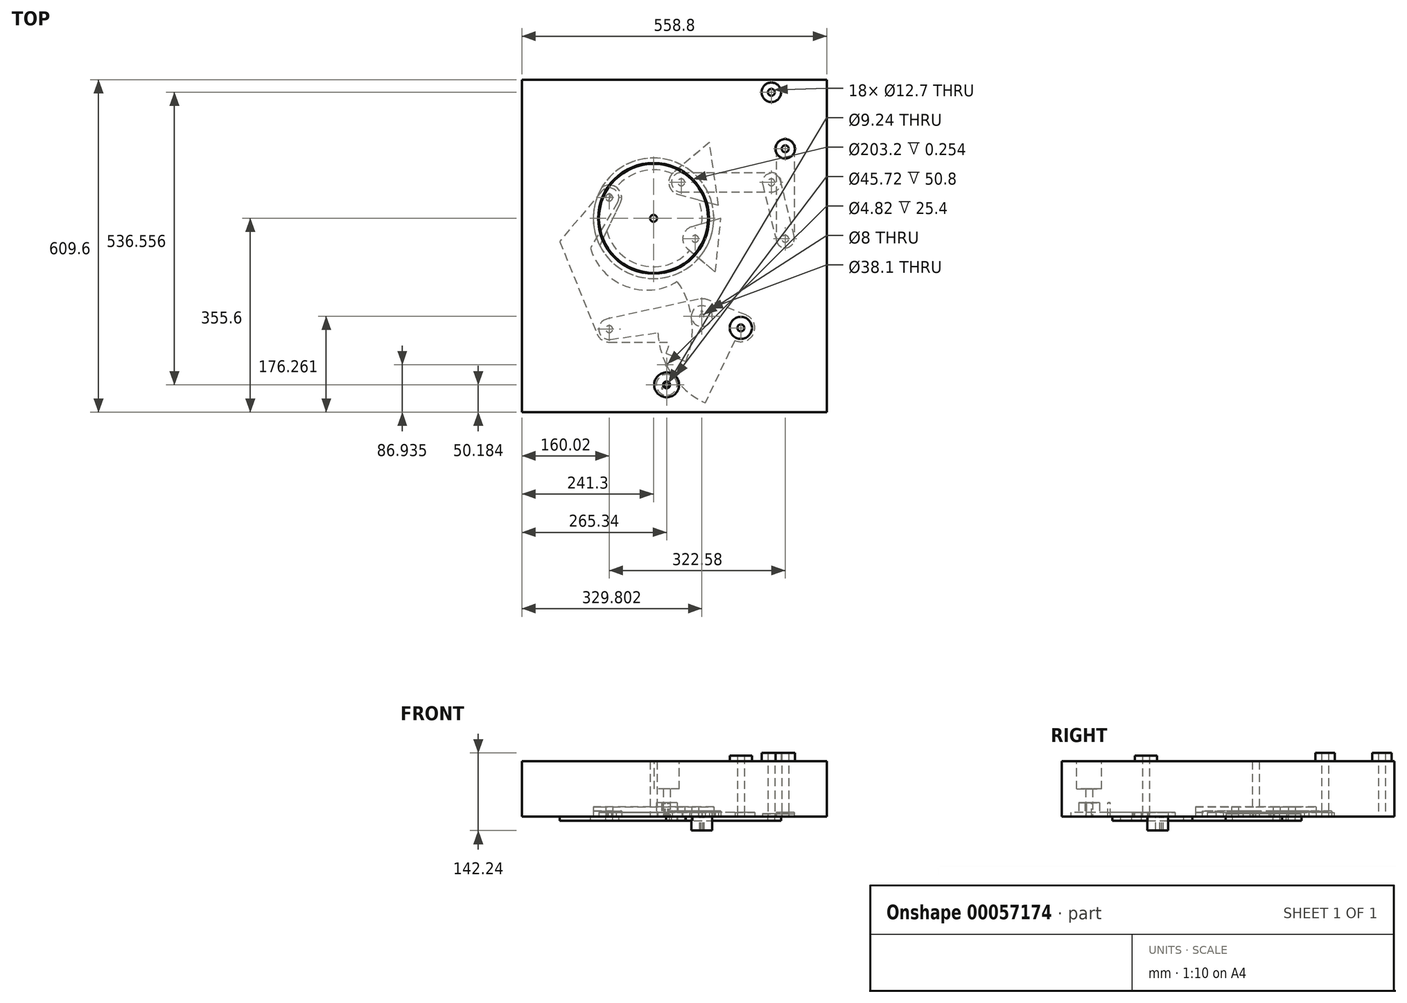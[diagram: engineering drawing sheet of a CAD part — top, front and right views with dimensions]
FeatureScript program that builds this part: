
annotation { "Feature Type Name" : "Feature", "Feature Type Description" : "" }
export const myFeature = defineFeature(function(context is Context, id is Id, definition is map)
    precondition{}
    {
        {
            var Q0;
            Q0=qCreatedBy(makeId("Top.planeOp"),FACE);
            var sketch = newSketch(context, id + "F0", { "sketchPlane" : qUnion([Q0])});
            skCircle(sketch, "E0", {"center": v(0, 0) * mm, "radius": 100 * mm});
            skCircle(sketch, "E1", {"center": v(-100, 0) * mm, "radius": 100 * mm, "construction": true});
            skCircle(sketch, "E2", {"center": v(0, 100) * mm, "radius": 100 * mm, "construction": true});
            skCircle(sketch, "E3", {"center": v(100, 0) * mm, "radius": 100 * mm, "construction": true});
            skCircle(sketch, "E4", {"center": v(0, -100) * mm, "radius": 100 * mm, "construction": true});
            skLineSegment(sketch, "E5", {"start": v(0, 0) * mm, "end": v(0, 167.8) * mm, "construction": true});
            skLineSegment(sketch, "E6", {"start": v(-81.28, 38.1) * mm, "end": v(-81.28, -203.2) * mm, "construction": true});
            skLineSegment(sketch, "E7", {"start": v(-81.28, -203.2) * mm, "end": v(160, -200.98) * mm, "construction": true});
            skLineSegment(sketch, "E8", {"start": v(-81.28, 38.1) * mm, "end": v(160, -200.98) * mm, "construction": true});
            skArc(sketch, "E9", {"start": v(24.5, 13.68) * mm, "mid": v(-74.9, 38.02) * mm, "end": v(-175.43, 18.97) * mm, "construction": true});
            skArc(sketch, "E10", {"start": v(-57.83, -97.2) * mm, "mid": v(-81.25, -196.81) * mm, "end": v(-61.29, -297.17) * mm, "construction": true});
            skLineSegment(sketch, "E11", {"start": v(-175.43, 18.97) * mm, "end": v(-81.28, -203.2) * mm, "construction": true});
            skLineSegment(sketch, "E12", {"start": v(24.5, 13.68) * mm, "end": v(-81.28, -203.2) * mm, "construction": true});
            skLineSegment(sketch, "E13", {"start": v(-61.29, -297.17) * mm, "end": v(160, -200.98) * mm, "construction": true});
            skLineSegment(sketch, "E14", {"start": v(-57.83, -97.2) * mm, "end": v(160, -200.98) * mm, "construction": true});
            skLineSegment(sketch, "E15", {"start": v(-175.43, 18.97) * mm, "end": v(24.5, 13.68) * mm, "construction": true});
            skLineSegment(sketch, "E16", {"start": v(-57.83, -97.2) * mm, "end": v(-61.29, -297.17) * mm, "construction": true});
            skCircle(sketch, "E17", {"center": v(0, 0) * mm, "radius": 200 * mm, "construction": true});
            skLineSegment(sketch, "E18", {"start": v(50.8, 66.04) * mm, "end": v(215.9, 66.04) * mm, "construction": true});
            skLineSegment(sketch, "E19", {"start": v(215.9, 66.04) * mm, "end": v(215.9, 231.14) * mm, "construction": true});
            skLineSegment(sketch, "E20", {"start": v(76.2, -37.57) * mm, "end": v(241.3, -37.57) * mm, "construction": true});
            skLineSegment(sketch, "E21", {"start": v(241.3, -37.57) * mm, "end": v(241.3, 127.53) * mm, "construction": true});
            skLineSegment(sketch, "E22", {"start": v(50.8, 66.04) * mm, "end": v(76.2, -37.57) * mm, "construction": true});
            skLineSegment(sketch, "E23", {"start": v(215.9, 231.14) * mm, "end": v(241.3, 127.53) * mm, "construction": true});
            skLineSegment(sketch, "E24", {"start": v(215.9, 66.04) * mm, "end": v(241.3, -37.57) * mm, "construction": true});
            skSolve(sketch);
        }
        {
            var Q0;
            Q0=qCreatedBy(makeId("Top.planeOp"),FACE);
            var sketch = newSketch(context, id + "F1", { "sketchPlane" : qUnion([Q0])});
            skCircle(sketch, "E25", {"center": v(-81.28, 38.1) * mm, "radius": 17.78 * mm});
            skCircle(sketch, "E26", {"center": v(-81.28, -203.2) * mm, "radius": 23.86 * mm});
            skArc(sketch, "E27", {"start": v(59, -262.75) * mm, "mid": v(70.29, -187.27) * mm, "end": v(43.56, -115.79) * mm});
            skLineSegment(sketch, "E28", {"start": v(-81.28, -203.2) * mm, "end": v(43.56, -115.79) * mm, "construction": true});
            skLineSegment(sketch, "E29", {"start": v(-81.28, -203.2) * mm, "end": v(62.82, -252.82) * mm, "construction": true});
            skLineSegment(sketch, "E30", {"start": v(-66, 29.02) * mm, "end": v(-115.73, -54.74) * mm});
            skCircle(sketch, "E31", {"center": v(88.5, -179.34) * mm, "radius": 19.05 * mm});
            skLineSegment(sketch, "E32", {"start": v(88.5, -179.34) * mm, "end": v(-81.28, -203.2) * mm});
            skLineSegment(sketch, "E33", {"start": v(-94.9, 49.53) * mm, "end": v(-172, -42.36) * mm});
            skLineSegment(sketch, "E34", {"start": v(-172, -42.36) * mm, "end": v(-103.4, -212.14) * mm});
            skArc(sketch, "E35", {"start": v(-115.73, -54.74) * mm, "mid": v(-51.14, -124.55) * mm, "end": v(43.56, -115.79) * mm});
            skLineSegment(sketch, "E36", {"start": v(-81.28, -227.06) * mm, "end": v(29.52, -227.06) * mm});
            skArc(sketch, "E37", {"start": v(23.05, -247.49) * mm, "mid": v(26.77, -237.43) * mm, "end": v(29.52, -227.06) * mm});
            skLineSegment(sketch, "E38.trimOffspring", {"start": v(23.05, -247.49) * mm, "end": v(59, -262.75) * mm});
            skCircle(sketch, "E39", {"center": v(-81.28, -203.2) * mm, "radius": 6.35 * mm});
            skCircle(sketch, "E40", {"center": v(-81.28, 38.1) * mm, "radius": 6.35 * mm});
            skSolve(sketch);
        }
        {
            var Q0;
            Q0=qCreatedBy(makeId("Top.planeOp"),FACE);
            var sketch = newSketch(context, id + "F2", { "sketchPlane" : qUnion([Q0])});
            skCircle(sketch, "E41", {"center": v(160, -200.98) * mm, "radius": 25.4 * mm});
            skCircle(sketch, "E42", {"center": v(-81.28, -203.2) * mm, "radius": 19.05 * mm});
            skArc(sketch, "E43", {"start": v(7.87, -209.9) * mm, "mid": v(33.58, -286.07) * mm, "end": v(94.47, -338.56) * mm});
            skCircle(sketch, "E44", {"center": v(24.04, -305.42) * mm, "radius": 19.05 * mm});
            skLineSegment(sketch, "E45", {"start": v(160, -200.98) * mm, "end": v(24.04, -305.42) * mm, "construction": true});
            skLineSegment(sketch, "E46", {"start": v(10.18, -228.82) * mm, "end": v(160, -200.98) * mm, "construction": true});
            skCircle(sketch, "E47", {"center": v(88.5, -179.34) * mm, "radius": 31.75 * mm});
            skLineSegment(sketch, "E48", {"start": v(169.4, -177.38) * mm, "end": v(100.25, -149.84) * mm});
            skLineSegment(sketch, "E49", {"start": v(81.77, -148.31) * mm, "end": v(-85.32, -184.58) * mm});
            skLineSegment(sketch, "E50", {"start": v(-78.63, -222.06) * mm, "end": v(7.87, -209.9) * mm});
            skCircle(sketch, "E51", {"center": v(160, -200.98) * mm, "radius": 6.35 * mm});
            skCircle(sketch, "E52", {"center": v(88.5, -179.34) * mm, "radius": 19.05 * mm});
            skCircle(sketch, "E53", {"center": v(-81.28, -203.2) * mm, "radius": 6.35 * mm});
            skLineSegment(sketch, "E54", {"start": v(-81.28, -203.2) * mm, "end": v(88.5, -179.34) * mm, "construction": true});
            skLineSegment(sketch, "E55.trimOffspring", {"start": v(149.09, -223.9) * mm, "end": v(94.47, -338.56) * mm});
            skCircle(sketch, "E56", {"center": v(15.96, -311.62) * mm, "radius": 1.52 * mm});
            skCircle(sketch, "E57", {"center": v(24.04, -305.42) * mm, "radius": 4 * mm});
            skSolve(sketch);
        }
        {
            var Q0;
            Q0=qCreatedBy(makeId("Top.planeOp"),FACE);
            var sketch = newSketch(context, id + "F3", { "sketchPlane" : qUnion([Q0])});
            skLineSegment(sketch, "E58.bottom", {"start": v(-241.3, 254) * mm, "end": v(317.5, 254) * mm});
            skLineSegment(sketch, "E58.top", {"start": v(-241.3, -355.6) * mm, "end": v(317.5, -355.6) * mm});
            skLineSegment(sketch, "E58.left", {"start": v(-241.3, 254) * mm, "end": v(-241.3, -355.6) * mm});
            skLineSegment(sketch, "E58.right", {"start": v(317.5, 254) * mm, "end": v(317.5, -355.6) * mm});
            skCircle(sketch, "E59", {"center": v(24.04, -305.42) * mm, "radius": 6.35 * mm});
            skCircle(sketch, "E60", {"center": v(160, -200.98) * mm, "radius": 6.35 * mm});
            skCircle(sketch, "E61", {"center": v(0, 0) * mm, "radius": 6.35 * mm});
            skCircle(sketch, "E62", {"center": v(215.9, 231.14) * mm, "radius": 6.35 * mm});
            skCircle(sketch, "E63", {"center": v(241.3, 127.53) * mm, "radius": 6.35 * mm});
            skSolve(sketch);
        }
        {
            var Q0;
            {var subQ8=sQuery(id+"F1.wireOp",EDGE,"E30");Q0=makeQuery(id+"F1.imprint","IMPRINT",FACE,{"disambiguationData":[TD([[makeQuery(id+"F1.imprint","IMPRINT",EDGE,{"derivedFrom":subQ8}),-1.0]])]});}
            var Q1;
            {var subQ1=sQuery(id+"F1.wireOp",EDGE,"E36");Q1=makeQuery(id+"F1.imprint","IMPRINT",FACE,{"disambiguationData":[TD([[makeQuery(id+"F1.imprint","IMPRINT",EDGE,{"derivedFrom":subQ1}),1.0]])]});}
            var Q2;
            Q2=makeQuery(id+"F1.imprint","IMPRINT",FACE,{"disambiguationData":[TD([[makeQuery(id+"F1.imprint","IMPRINT",EDGE,{"derivedFrom":sQuery(id+"F1.wireOp",EDGE,"E39")}),-1.0]])]});
            var Q3;
            Q3=makeQuery(id+"F1.imprint","IMPRINT",FACE,{"disambiguationData":[TD([[makeQuery(id+"F1.imprint","IMPRINT",EDGE,{"derivedFrom":sQuery(id+"F1.wireOp",EDGE,"E40")}),-1.0]])]});
            extrude(context, id + "F4", {"entities" : qUnion([Q0, Q1, Q2, Q3]), "oppositeDirection" : true, "depth" : 7.62 * mm});
        }
        {
            var Q0;
            Q0=makeQuery(id+"F1.imprint","IMPRINT",FACE,{"disambiguationData":[TD([[makeQuery(id+"F1.imprint","IMPRINT",EDGE,{"derivedFrom":sQuery(id+"F1.wireOp",EDGE,"E31")}),1.0]])]});
            extrude(context, id + "F5", {"entities" : qUnion([Q0]), "oppositeDirection" : true, "depth" : 25.4 * mm});
        }
        {
            var Q0;
            {var subQ3=sQuery(id+"F2.wireOp",EDGE,"E48");Q0=makeQuery(id+"F2.imprint","IMPRINT",FACE,{"disambiguationData":[TD([[makeQuery(id+"F2.imprint","IMPRINT",EDGE,{"derivedFrom":subQ3}),1.0]])]});}
            var Q1;
            Q1=makeQuery(id+"F2.imprint","IMPRINT",FACE,{"disambiguationData":[TD([[makeQuery(id+"F2.imprint","IMPRINT",EDGE,{"derivedFrom":sQuery(id+"F2.wireOp",EDGE,"E53")}),-1.0]])]});
            var Q2;
            Q2=makeQuery(id+"F2.imprint","IMPRINT",FACE,{"disambiguationData":[TD([[makeQuery(id+"F2.imprint","IMPRINT",EDGE,{"derivedFrom":sQuery(id+"F2.wireOp",EDGE,"E52")}),-1.0]])]});
            var Q3;
            Q3=makeQuery(id+"F2.imprint","IMPRINT",FACE,{"disambiguationData":[TD([[makeQuery(id+"F2.imprint","IMPRINT",EDGE,{"derivedFrom":sQuery(id+"F2.wireOp",EDGE,"E51")}),-1.0]])]});
            extrude(context, id + "F6", {"entities" : qUnion([Q0, Q1, Q2, Q3]), "depth" : 7.62 * mm});
        }
        {
            var Q0;
            Q0=makeQuery(id+"F2.imprint","IMPRINT",FACE,{"disambiguationData":[TD([[makeQuery(id+"F2.imprint","IMPRINT",EDGE,{"derivedFrom":sQuery(id+"F2.wireOp",EDGE,"E44")}),1.0]])]});
            extrude(context, id + "F7", {"entities" : qUnion([Q0]), "depth" : 25.4 * mm});
        }
        {
            var Q0;
            Q0=makeQuery(id+"F3.imprint","IMPRINT",FACE,{"disambiguationData":[TD([[makeQuery(id+"F3.imprint","IMPRINT",EDGE,{"derivedFrom":sQuery(id+"F3.wireOp",EDGE,"E58.bottom")}),-1.0]])]});
            extrude(context, id + "F8", {"entities" : qUnion([Q0]), "depth" : 101.6 * mm});
        }
        {
            var Q0;
            Q0=makeQuery(id+"F8.opExtrude","CAP_FACE",FACE,{"disambiguationData":[OSD([sQuery(id+"F3.wireOp",EDGE,"E58.bottom"),sQuery(id+"F3.wireOp",EDGE,"E58.top"),sQuery(id+"F3.wireOp",EDGE,"E58.left"),sQuery(id+"F3.wireOp",EDGE,"E58.right"),sQuery(id+"F3.wireOp",EDGE,"E59"),sQuery(id+"F3.wireOp",EDGE,"E60"),sQuery(id+"F3.wireOp",EDGE,"E61")])],"isStart":false});
            var sketch = newSketch(context, id + "F9", { "sketchPlane" : qUnion([Q0])});
            skCircle(sketch, "E64", {"center": v(0, 0) * mm, "radius": 101.6 * mm});
            skCircle(sketch, "E65", {"center": v(0, 0) * mm, "radius": 100 * mm});
            skSolve(sketch);
        }
        {
            var Q0;
            Q0=qSketchRegion(id+"F9",true);
            extrude(context, id + "F10", {"entities" : qUnion([Q0]), "operationType" : NewBodyOperationType.REMOVE, "oppositeDirection" : true, "depth" : 0.25 * mm});
        }
        {
            var Q0;
            {var subQ0=sQuery(id+"F3.wireOp",EDGE,"E58.bottom");var subQ1=sQuery(id+"F3.wireOp",EDGE,"E58.top");var subQ2=sQuery(id+"F3.wireOp",EDGE,"E58.left");var subQ3=sQuery(id+"F3.wireOp",EDGE,"E58.right");var subQ4=sQuery(id+"F3.wireOp",EDGE,"E59");var subQ5=sQuery(id+"F3.wireOp",EDGE,"E60");Q0=makeQuery(id+"F10.boolean.opBoolean","SPLIT",FACE,{"disambiguationData":[TD([makeQuery(id+"F8.opExtrude","SWEPT_FACE",FACE,{"disambiguationData":[OSD([subQ0])]})])],"derivedFrom":makeQuery(id+"F8.opExtrude","CAP_FACE",FACE,{"disambiguationData":[OSD([subQ0,subQ1,subQ2,subQ3,subQ4,subQ5,sQuery(id+"F3.wireOp",EDGE,"E61")])],"isStart":false})});}
            var sketch = newSketch(context, id + "F11", { "sketchPlane" : qUnion([Q0])});
            skCircle(sketch, "E66", {"center": v(160, -200.98) * mm, "radius": 20.32 * mm});
            skCircle(sketch, "E67", {"center": v(160, -200.98) * mm, "radius": 6.35 * mm});
            skSolve(sketch);
        }
        {
            var Q0;
            Q0=qSketchRegion(id+"F11",true);
            extrude(context, id + "F12", {"entities" : qUnion([Q0]), "operationType" : NewBodyOperationType.ADD, "depth" : 10.16 * mm});
        }
        {
            var Q0;
            {var subQ0=sQuery(id+"F3.wireOp",EDGE,"E58.bottom");var subQ1=sQuery(id+"F3.wireOp",EDGE,"E58.top");var subQ2=sQuery(id+"F3.wireOp",EDGE,"E58.left");var subQ3=sQuery(id+"F3.wireOp",EDGE,"E58.right");var subQ4=sQuery(id+"F3.wireOp",EDGE,"E59");var subQ5=sQuery(id+"F3.wireOp",EDGE,"E60");Q0=makeQuery(id+"F10.boolean.opBoolean","SPLIT",FACE,{"disambiguationData":[TD([makeQuery(id+"F8.opExtrude","SWEPT_FACE",FACE,{"disambiguationData":[OSD([subQ0])]})])],"derivedFrom":makeQuery(id+"F8.opExtrude","CAP_FACE",FACE,{"disambiguationData":[OSD([subQ0,subQ1,subQ2,subQ3,subQ4,subQ5,sQuery(id+"F3.wireOp",EDGE,"E61")])],"isStart":false})});}
            var sketch = newSketch(context, id + "F13", { "sketchPlane" : qUnion([Q0])});
            skCircle(sketch, "E68", {"center": v(24.04, -305.42) * mm, "radius": 22.86 * mm});
            skSolve(sketch);
        }
        {
            var Q0;
            Q0=qSketchRegion(id+"F13",true);
            extrude(context, id + "F14", {"entities" : qUnion([Q0]), "operationType" : NewBodyOperationType.REMOVE, "oppositeDirection" : true, "depth" : 50.8 * mm});
        }
        {
            var Q0;
            Q0=makeQuery(id+"F7.opExtrude","CAP_FACE",FACE,{"disambiguationData":[OSD([sQuery(id+"F2.wireOp",EDGE,"E44")])],"isStart":false});
            var sketch = newSketch(context, id + "F15", { "sketchPlane" : qUnion([Q0])});
            skCircle(sketch, "E69", {"center": v(24.04, -305.42) * mm, "radius": 4.62 * mm});
            skCircle(sketch, "E70", {"center": v(24.04, -268.67) * mm, "radius": 2.41 * mm});
            skSolve(sketch);
        }
        {
            var Q0;
            Q0=qSketchRegion(id+"F15",true);
            extrude(context, id + "F16", {"entities" : qUnion([Q0]), "operationType" : NewBodyOperationType.REMOVE, "endBound" : BoundingType.THROUGH_ALL, "oppositeDirection" : true, "depth" : 25.4 * mm});
        }
        {
            var Q0;
            Q0=makeQuery(id+"F5.opExtrude","CAP_FACE",FACE,{"disambiguationData":[OSD([sQuery(id+"F1.wireOp",EDGE,"E31")])],"isStart":true});
            var sketch = newSketch(context, id + "F17", { "sketchPlane" : qUnion([Q0])});
            skCircle(sketch, "E71", {"center": v(88.5, -179.34) * mm, "radius": 4 * mm});
            skCircle(sketch, "E72", {"center": v(88.5, -170.8) * mm, "radius": 1.52 * mm});
            skLineSegment(sketch, "E73", {"start": v(88.5, -179.34) * mm, "end": v(88.5, -211.92) * mm, "construction": true});
            skSolve(sketch);
        }
        {
            var Q0;
            Q0=qSketchRegion(id+"F17",true);
            extrude(context, id + "F18", {"entities" : qUnion([Q0]), "operationType" : NewBodyOperationType.REMOVE, "endBound" : BoundingType.THROUGH_ALL, "oppositeDirection" : true, "depth" : 25.4 * mm});
        }
        {
            var Q0;
            Q0=qCreatedBy(makeId("Top.planeOp"),FACE);
            var sketch = newSketch(context, id + "F19", { "sketchPlane" : qUnion([Q0])});
            skCircle(sketch, "E74", {"center": v(0, 0) * mm, "radius": 110.5 * mm});
            skCircle(sketch, "E75", {"center": v(-81.28, 38.1) * mm, "radius": 6.35 * mm});
            skCircle(sketch, "E76", {"center": v(50.8, 66.04) * mm, "radius": 6.35 * mm});
            skCircle(sketch, "E77", {"center": v(76.2, -37.57) * mm, "radius": 6.35 * mm});
            skSolve(sketch);
        }
        {
            var Q0;
            Q0=qSketchRegion(id+"F19",true);
            extrude(context, id + "F20", {"entities" : qUnion([Q0]), "depth" : 17.78 * mm});
        }
        {
            var Q0;
            Q0=makeQuery(id+"F20.opExtrude","CAP_FACE",FACE,{"disambiguationData":[OSD([sQuery(id+"F19.wireOp",EDGE,"E74"),sQuery(id+"F19.wireOp",EDGE,"E75")])],"isStart":true});
            var sketch = newSketch(context, id + "F21", { "sketchPlane" : qUnion([Q0])});
            skCircle(sketch, "E78", {"center": v(-81.28, -38.1) * mm, "radius": 22.86 * mm});
            skLineSegment(sketch, "E79", {"start": v(-98.6, 49.85) * mm, "end": v(-60.72, -28.1) * mm});
            skArc(sketch, "E80", {"start": v(-98.6, 49.85) * mm, "mid": v(-110.43, -3.71) * mm, "end": v(-95.04, -56.36) * mm});
            skLineSegment(sketch, "E81", {"start": v(0, 0) * mm, "end": v(-64.6, 0) * mm});
            skSolve(sketch);
        }
        {
            var Q0;
            Q0=makeQuery(id+"F21.imprint","IMPRINT",FACE,{"disambiguationData":[TD([[makeQuery(id+"F21.imprint","IMPRINT",EDGE,{"derivedFrom":makeQuery(id+"F20.opExtrude","CAP_EDGE",EDGE,{"disambiguationData":[OSD([sQuery(id+"F19.wireOp",EDGE,"E75")])],"isStart":true})}),1.0]])]});
            var Q1;
            {var subQ3=sQuery(id+"F21.wireOp",EDGE,"E79");Q1=makeQuery(id+"F21.imprint","IMPRINT",FACE,{"disambiguationData":[TD([[makeQuery(id+"F21.imprint","IMPRINT",EDGE,{"derivedFrom":subQ3}),-1.0]])]});}
            extrude(context, id + "F22", {"entities" : qUnion([Q0, Q1]), "operationType" : NewBodyOperationType.REMOVE, "oppositeDirection" : true, "depth" : 10.16 * mm});
        }
        {
            var Q0;
            Q0=makeQuery(id+"F20.opExtrude","CAP_FACE",FACE,{"disambiguationData":[OSD([sQuery(id+"F19.wireOp",EDGE,"E74"),sQuery(id+"F19.wireOp",EDGE,"E75")])],"isStart":true});
            var sketch = newSketch(context, id + "F23", { "sketchPlane" : qUnion([Q0])});
            skCircle(sketch, "E82", {"center": v(0, 0) * mm, "radius": 88.9 * mm});
            skCircle(sketch, "E83", {"center": v(0, 0) * mm, "radius": 110.5 * mm});
            skSolve(sketch);
        }
        {
            var Q0;
            Q0=qSketchRegion(id+"F23",true);
            extrude(context, id + "F24", {"entities" : qUnion([Q0]), "operationType" : NewBodyOperationType.REMOVE, "oppositeDirection" : true, "depth" : 7.62 * mm});
        }
        {
            var Q0;
            Q0=qCreatedBy(makeId("Top.planeOp"),FACE);
            var sketch = newSketch(context, id + "F25", { "sketchPlane" : qUnion([Q0])});
            skCircle(sketch, "E84", {"center": v(50.8, 66.04) * mm, "radius": 17.78 * mm});
            skCircle(sketch, "E85", {"center": v(215.9, 66.04) * mm, "radius": 17.78 * mm});
            skLineSegment(sketch, "E86", {"start": v(50.8, 83.82) * mm, "end": v(215.9, 83.82) * mm});
            skLineSegment(sketch, "E87", {"start": v(50.8, 48.26) * mm, "end": v(215.9, 48.26) * mm});
            skCircle(sketch, "E88", {"center": v(50.8, 66.04) * mm, "radius": 6.35 * mm});
            skCircle(sketch, "E89", {"center": v(215.9, 66.04) * mm, "radius": 6.35 * mm});
            skSolve(sketch);
        }
        {
            var Q0;
            Q0=qCreatedBy(makeId("Top.planeOp"),FACE);
            var sketch = newSketch(context, id + "F26", { "sketchPlane" : qUnion([Q0])});
            skCircle(sketch, "E90", {"center": v(241.3, -37.57) * mm, "radius": 16.5 * mm});
            skCircle(sketch, "E91", {"center": v(241.3, 127.53) * mm, "radius": 16.51 * mm});
            skLineSegment(sketch, "E92", {"start": v(257.81, 127.53) * mm, "end": v(257.8, -37.57) * mm});
            skLineSegment(sketch, "E93", {"start": v(224.8, 127.53) * mm, "end": v(224.8, -37.57) * mm});
            skCircle(sketch, "E94", {"center": v(241.3, 127.53) * mm, "radius": 6.35 * mm});
            skCircle(sketch, "E95", {"center": v(241.3, -37.57) * mm, "radius": 6.35 * mm});
            skSolve(sketch);
        }
        {
            var Q0;
            Q0=qCreatedBy(makeId("Top.planeOp"),FACE);
            var sketch = newSketch(context, id + "F27", { "sketchPlane" : qUnion([Q0])});
            skCircle(sketch, "E96", {"center": v(215.9, 66.04) * mm, "radius": 16.51 * mm});
            skCircle(sketch, "E97", {"center": v(241.3, -37.57) * mm, "radius": 16.51 * mm});
            skLineSegment(sketch, "E98", {"start": v(231.94, 69.97) * mm, "end": v(257.34, -33.64) * mm});
            skLineSegment(sketch, "E99", {"start": v(199.86, 62.1) * mm, "end": v(225.26, -41.5) * mm});
            skCircle(sketch, "E100", {"center": v(215.9, 66.04) * mm, "radius": 6.35 * mm});
            skCircle(sketch, "E101", {"center": v(241.3, -37.57) * mm, "radius": 6.35 * mm});
            skSolve(sketch);
        }
        {
            var Q0;
            Q0=makeQuery(id+"F25.imprint","IMPRINT",FACE,{"disambiguationData":[TD([[makeQuery(id+"F25.imprint","IMPRINT",EDGE,{"derivedFrom":sQuery(id+"F25.wireOp",EDGE,"E89")}),-1.0]])]});
            var Q1;
            {var subQ1=sQuery(id+"F25.wireOp",EDGE,"E86");Q1=makeQuery(id+"F25.imprint","IMPRINT",FACE,{"disambiguationData":[TD([[makeQuery(id+"F25.imprint","IMPRINT",EDGE,{"derivedFrom":subQ1}),-1.0]])]});}
            var Q2;
            Q2=makeQuery(id+"F25.imprint","IMPRINT",FACE,{"disambiguationData":[TD([[makeQuery(id+"F25.imprint","IMPRINT",EDGE,{"derivedFrom":sQuery(id+"F25.wireOp",EDGE,"E88")}),-1.0]])]});
            extrude(context, id + "F28", {"entities" : qUnion([Q0, Q1, Q2]), "oppositeDirection" : true, "depth" : 7.62 * mm});
        }
        {
            var Q0;
            Q0=makeQuery(id+"F26.imprint","IMPRINT",FACE,{"disambiguationData":[TD([[makeQuery(id+"F26.imprint","IMPRINT",EDGE,{"derivedFrom":sQuery(id+"F26.wireOp",EDGE,"E94")}),-1.0]])]});
            var Q1;
            {var subQ1=sQuery(id+"F26.wireOp",EDGE,"E92");Q1=makeQuery(id+"F26.imprint","IMPRINT",FACE,{"disambiguationData":[TD([[makeQuery(id+"F26.imprint","IMPRINT",EDGE,{"derivedFrom":subQ1}),-1.0]])]});}
            var Q2;
            Q2=makeQuery(id+"F26.imprint","IMPRINT",FACE,{"disambiguationData":[TD([[makeQuery(id+"F26.imprint","IMPRINT",EDGE,{"derivedFrom":sQuery(id+"F26.wireOp",EDGE,"E95")}),-1.0]])]});
            extrude(context, id + "F29", {"entities" : qUnion([Q0, Q1, Q2]), "depth" : 7.62 * mm});
        }
        {
            var Q0;
            Q0=makeQuery(id+"F27.imprint","IMPRINT",FACE,{"disambiguationData":[TD([[makeQuery(id+"F27.imprint","IMPRINT",EDGE,{"derivedFrom":sQuery(id+"F27.wireOp",EDGE,"E100")}),-1.0]])]});
            var Q1;
            {var subQ0=sQuery(id+"F27.wireOp",EDGE,"E98");Q1=makeQuery(id+"F27.imprint","IMPRINT",FACE,{"disambiguationData":[TD([[makeQuery(id+"F27.imprint","IMPRINT",EDGE,{"derivedFrom":subQ0}),-1.0]])]});}
            var Q2;
            Q2=makeQuery(id+"F27.imprint","IMPRINT",FACE,{"disambiguationData":[TD([[makeQuery(id+"F27.imprint","IMPRINT",EDGE,{"derivedFrom":sQuery(id+"F27.wireOp",EDGE,"E101")}),-1.0]])]});
            extrude(context, id + "F30", {"entities" : qUnion([Q0, Q1, Q2]), "depth" : 5.08 * mm});
        }
        {
            var Q0;
            {var subQ0=sQuery(id+"F3.wireOp",EDGE,"E58.bottom");var subQ1=sQuery(id+"F3.wireOp",EDGE,"E58.top");var subQ2=sQuery(id+"F3.wireOp",EDGE,"E58.left");var subQ3=sQuery(id+"F3.wireOp",EDGE,"E58.right");var subQ4=sQuery(id+"F3.wireOp",EDGE,"E59");var subQ5=sQuery(id+"F3.wireOp",EDGE,"E60");var subQ6=sQuery(id+"F3.wireOp",EDGE,"E62");var subQ7=sQuery(id+"F3.wireOp",EDGE,"E63");Q0=makeQuery(id+"F10.boolean.opBoolean","SPLIT",FACE,{"disambiguationData":[TD([makeQuery(id+"F8.opExtrude","SWEPT_FACE",FACE,{"disambiguationData":[OSD([subQ0])]})])],"derivedFrom":makeQuery(id+"F8.opExtrude","CAP_FACE",FACE,{"disambiguationData":[OSD([subQ0,subQ1,subQ2,subQ3,subQ4,subQ5,sQuery(id+"F3.wireOp",EDGE,"E61"),subQ6,subQ7])],"isStart":false})});}
            var sketch = newSketch(context, id + "F31", { "sketchPlane" : qUnion([Q0])});
            skCircle(sketch, "E102", {"center": v(241.3, 127.53) * mm, "radius": 17.78 * mm});
            skCircle(sketch, "E103", {"center": v(215.9, 231.14) * mm, "radius": 17.78 * mm});
            skSolve(sketch);
        }
        {
            var Q0;
            Q0=makeQuery(id+"F31.imprint","IMPRINT",FACE,{"disambiguationData":[TD([[makeQuery(id+"F31.imprint","IMPRINT",EDGE,{"derivedFrom":sQuery(id+"F31.wireOp",EDGE,"E102")}),1.0]])]});
            var Q1;
            Q1=makeQuery(id+"F31.imprint","IMPRINT",FACE,{"disambiguationData":[TD([[makeQuery(id+"F31.imprint","IMPRINT",EDGE,{"derivedFrom":sQuery(id+"F31.wireOp",EDGE,"E103")}),1.0]])]});
            extrude(context, id + "F32", {"entities" : qUnion([Q0, Q1]), "operationType" : NewBodyOperationType.ADD, "depth" : 15.24 * mm});
        }
        {
            var Q0;
            Q0=qCreatedBy(makeId("Top.planeOp"),FACE);
            var sketch = newSketch(context, id + "F33", { "sketchPlane" : qUnion([Q0])});
            skCircle(sketch, "E104", {"center": v(76.2, -37.57) * mm, "radius": 22.86 * mm});
            skCircle(sketch, "E105", {"center": v(50.8, 66.04) * mm, "radius": 22.86 * mm});
            skLineSegment(sketch, "E106", {"start": v(61.5, -55.08) * mm, "end": v(113.22, -98.47) * mm});
            skLineSegment(sketch, "E107", {"start": v(113.22, -98.47) * mm, "end": v(123.54, -0.22) * mm});
            skLineSegment(sketch, "E108", {"start": v(123.54, -0.22) * mm, "end": v(69.9, -15.6) * mm});
            skLineSegment(sketch, "E109", {"start": v(76.2, -37.57) * mm, "end": v(142.68, -37.57) * mm, "construction": true});
            skLineSegment(sketch, "E110", {"start": v(44.88, 43.96) * mm, "end": v(118.75, 24.17) * mm});
            skLineSegment(sketch, "E111", {"start": v(118.75, 24.17) * mm, "end": v(102.57, 139.32) * mm});
            skLineSegment(sketch, "E112", {"start": v(102.57, 139.32) * mm, "end": v(36.1, 83.55) * mm});
            skLineSegment(sketch, "E113", {"start": v(50.8, 66.04) * mm, "end": v(139.65, 66.04) * mm, "construction": true});
            skSolve(sketch);
        }
        {
            var Q0;
            Q0=qSketchRegion(id+"F33",true);
            extrude(context, id + "F34", {"entities" : qUnion([Q0]), "operationType" : NewBodyOperationType.REMOVE, "depth" : 10.16 * mm});
        }
    });
